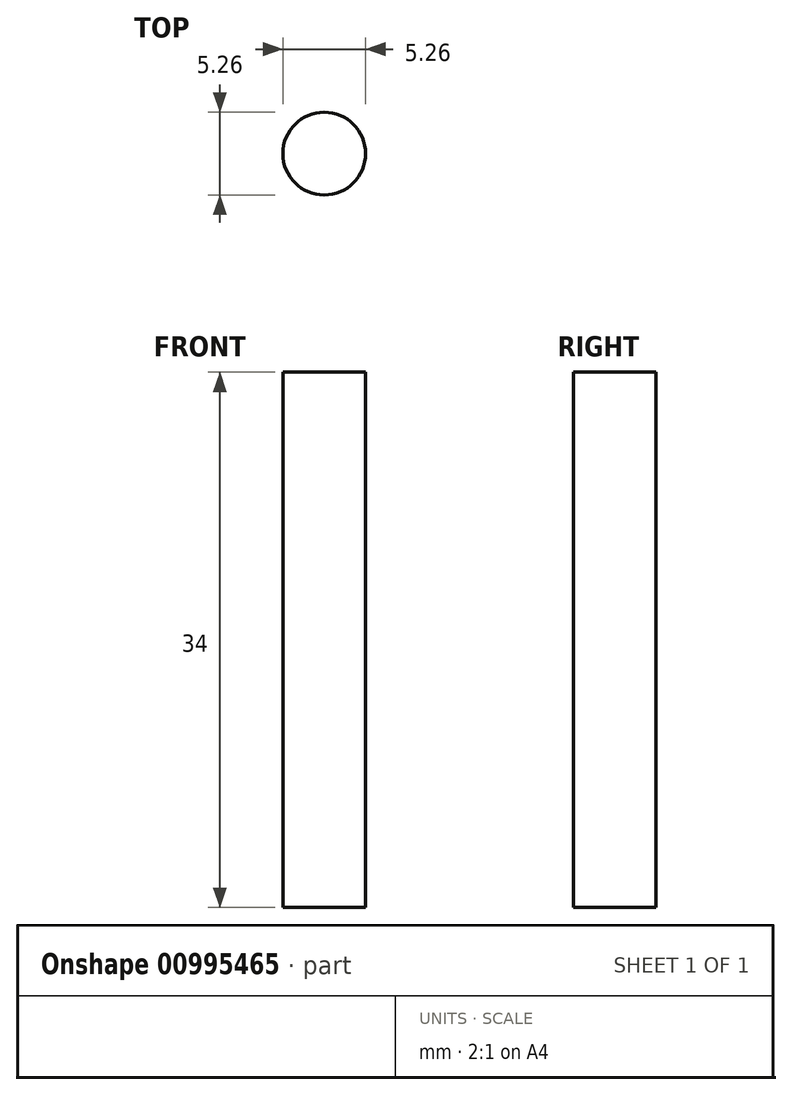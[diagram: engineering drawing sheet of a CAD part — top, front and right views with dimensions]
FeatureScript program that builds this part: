
annotation { "Feature Type Name" : "Feature", "Feature Type Description" : "" }
export const myFeature = defineFeature(function(context is Context, id is Id, definition is map)
    precondition{}
    {
        {
            var Q0;
            Q0=qCreatedBy(makeId("Top.planeOp"),FACE);
            var sketch = newSketch(context, id + "F0", { "sketchPlane" : qUnion([Q0])});
            skCircle(sketch, "E0", {"center": v(0, 0) * mm, "radius": 2.63 * mm});
            skSolve(sketch);
        }
        {
            var Q0;
            Q0=makeQuery(id+"F0.imprint","IMPRINT",FACE,{"disambiguationData":[TD([[makeQuery(id+"F0.imprint","IMPRINT",EDGE,{"derivedFrom":sQuery(id+"F0.wireOp",EDGE,"E0")}),1.0]])]});
            extrude(context, id + "F1", {"entities" : qUnion([Q0]), "depth" : 34 * mm, "offsetDistance" : 25 * mm});
        }
    });
